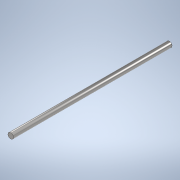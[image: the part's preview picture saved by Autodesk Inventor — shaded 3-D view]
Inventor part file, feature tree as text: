
AUTODESK INVENTOR PART (.ipt)
format: ipt  version: 2020 (Build 240168000, 168)  size: 94,208 bytes
history: native  units: mm
features: extrude x1, sketch x1
ambient origin geometry x8: Origin, YZ Plane, XZ Plane, XY Plane, X Axis, Y Axis, Z Axis, Center Point
bodies: Solid1 (feature_tree)
feature tree (2):
  extrude  "Extrusion1"  Depth=340.0mm TaperAngle=0.0deg
  sketch  "Sketch1"  dims[d0=12.0mm d1=340.0mm d2=0.0mm]
